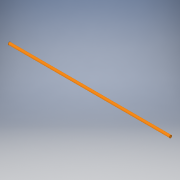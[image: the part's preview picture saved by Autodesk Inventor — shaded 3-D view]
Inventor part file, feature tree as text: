
AUTODESK INVENTOR PART (.ipt)
format: ipt  version: 2017 (Build 210142000, 142)  size: 88,576 bytes
history: native  units: in
note: dims shown in document units (in); Inventor stores cm internally (conversion verified against a paired STEP export)
features: extrude x1, sketch x1
ambient origin geometry x8: Origin, YZ Plane, XZ Plane, XY Plane, X Axis, Y Axis, Z Axis, Center Point
bodies: Solid1 (feature_tree)
feature tree (2):
  extrude  "Extrusion1"  Depth=20.0in TaperAngle=0.0deg
  sketch  "Sketch1"  dims[d0=0.3125in d1=20.0in d2=0.0in]
